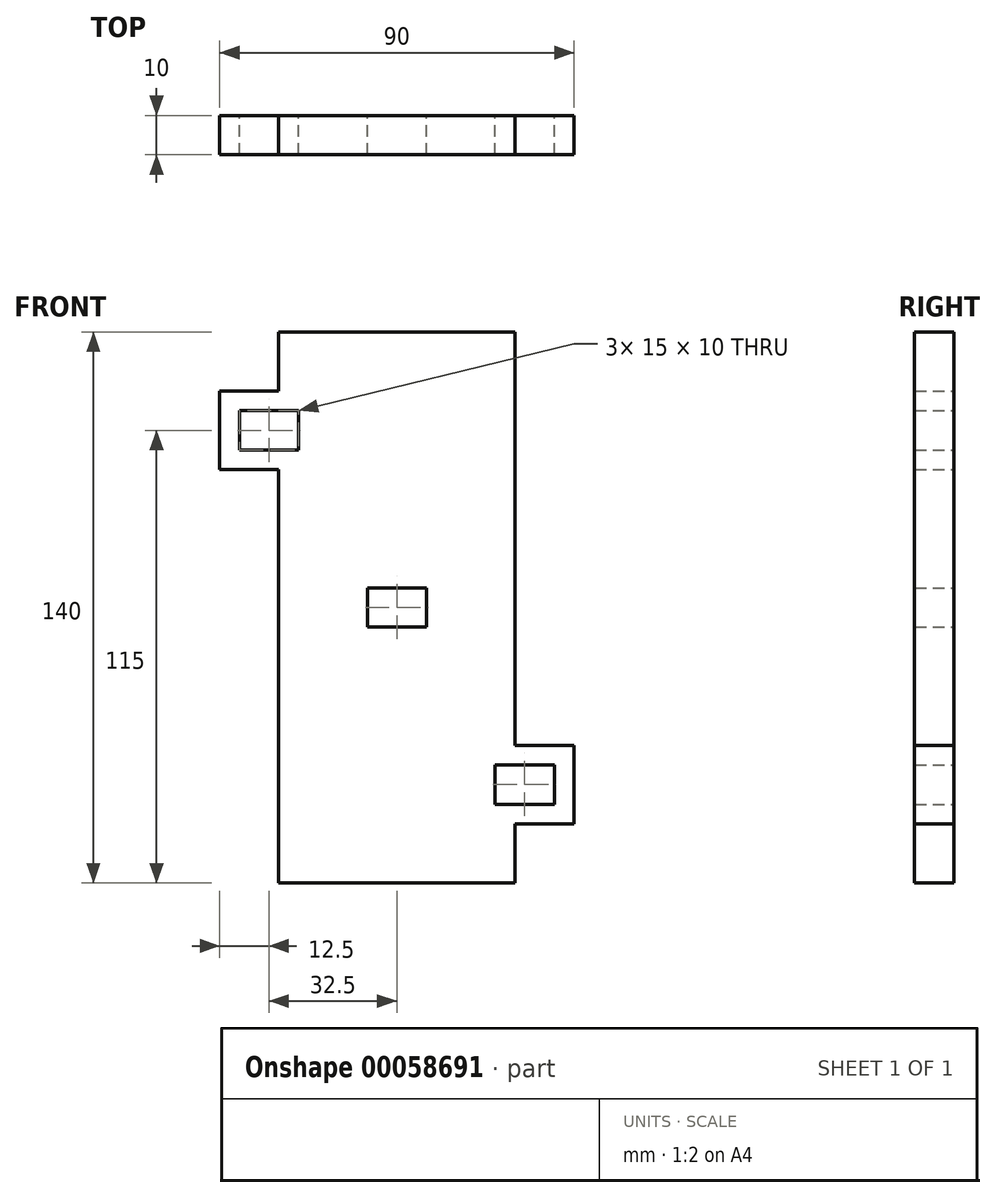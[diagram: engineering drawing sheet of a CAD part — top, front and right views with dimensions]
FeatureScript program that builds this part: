
annotation { "Feature Type Name" : "Feature", "Feature Type Description" : "" }
export const myFeature = defineFeature(function(context is Context, id is Id, definition is map)
    precondition{}
    {
        {
            var Q0;
            Q0=qCreatedBy(makeId("Front.planeOp"),FACE);
            var sketch = newSketch(context, id + "F0", { "sketchPlane" : qUnion([Q0])});
            skLineSegment(sketch, "E0.rect.bottom", {"start": v(-30, 70) * mm, "end": v(30, 70) * mm});
            skLineSegment(sketch, "E0.rect.top", {"start": v(-30, -70) * mm, "end": v(30, -70) * mm});
            skLineSegment(sketch, "E0.rect.right", {"start": v(30, 70) * mm, "end": v(30, -35) * mm});
            skPoint(sketch, "E0.rect.middle", {"position": v(0, 0) * mm});
            skLineSegment(sketch, "E1.bottom", {"start": v(-30, 55) * mm, "end": v(-45, 55) * mm});
            skLineSegment(sketch, "E1.top", {"start": v(-30, 35) * mm, "end": v(-45, 35) * mm});
            skLineSegment(sketch, "E1.right", {"start": v(-45, 55) * mm, "end": v(-45, 35) * mm});
            skLineSegment(sketch, "E2.bottom", {"start": v(30, -35) * mm, "end": v(45, -35) * mm});
            skLineSegment(sketch, "E2.top", {"start": v(30, -55) * mm, "end": v(45, -55) * mm});
            skLineSegment(sketch, "E2.right", {"start": v(45, -35) * mm, "end": v(45, -55) * mm});
            skLineSegment(sketch, "E3.rect.bottom", {"start": v(-7.5, 5) * mm, "end": v(7.5, 5) * mm});
            skLineSegment(sketch, "E3.rect.top", {"start": v(-7.5, -5) * mm, "end": v(7.5, -5) * mm});
            skLineSegment(sketch, "E3.rect.left", {"start": v(-7.5, 5) * mm, "end": v(-7.5, -5) * mm});
            skLineSegment(sketch, "E3.rect.right", {"start": v(7.5, 5) * mm, "end": v(7.5, -5) * mm});
            skLineSegment(sketch, "E4.trimOffspring", {"start": v(-30, 35) * mm, "end": v(-30, -70) * mm});
            skLineSegment(sketch, "E5.trimOffspring", {"start": v(30, -55) * mm, "end": v(30, -70) * mm});
            skLineSegment(sketch, "E6", {"start": v(-30, 70) * mm, "end": v(-30, 55) * mm});
            skPoint(sketch, "E7.oppositeSnap0", {"position": v(45, -45) * mm});
            skLineSegment(sketch, "E8.bottom", {"start": v(-40, 50) * mm, "end": v(-25, 50) * mm});
            skLineSegment(sketch, "E8.top", {"start": v(-40, 40) * mm, "end": v(-25, 40) * mm});
            skLineSegment(sketch, "E8.left", {"start": v(-40, 50) * mm, "end": v(-40, 40) * mm});
            skLineSegment(sketch, "E8.right", {"start": v(-25, 50) * mm, "end": v(-25, 40) * mm});
            skLineSegment(sketch, "E9.bottom", {"start": v(25, -40) * mm, "end": v(40, -40) * mm});
            skLineSegment(sketch, "E9.top", {"start": v(25, -50) * mm, "end": v(40, -50) * mm});
            skLineSegment(sketch, "E9.left", {"start": v(25, -40) * mm, "end": v(25, -50) * mm});
            skLineSegment(sketch, "E9.right", {"start": v(40, -40) * mm, "end": v(40, -50) * mm});
            skSolve(sketch);
        }
        {
            var Q0;
            Q0=makeQuery(id+"F0.imprint","IMPRINT",FACE,{"disambiguationData":[TD([[makeQuery(id+"F0.imprint","IMPRINT",EDGE,{"derivedFrom":sQuery(id+"F0.wireOp",EDGE,"E0.rect.bottom")}),-1.0]])]});
            extrude(context, id + "F1", {"entities" : qUnion([Q0]), "depth" : 10 * mm});
        }
    });
